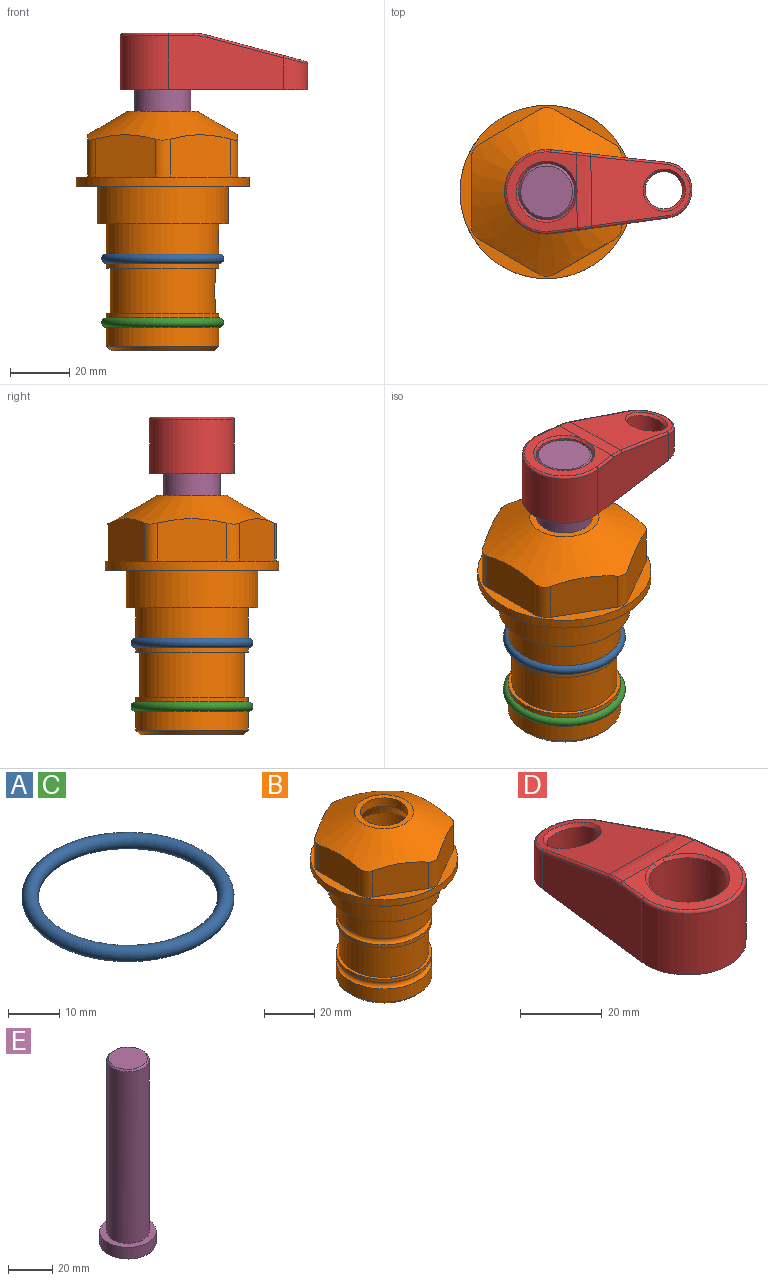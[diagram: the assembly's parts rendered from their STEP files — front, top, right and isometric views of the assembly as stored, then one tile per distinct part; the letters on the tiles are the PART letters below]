
ASSEMBLY  parts=5 mates=4
PART A: 1 faces, bbox 44.7x44.7x3.2 mm
  f0: torus R=19.05mm, axis (0,0,1), area 1193.9mm2
PART B: 36 faces, bbox 58.7x58.7x81 mm
  f0: cylinder r=17.78mm len=35.56mm, axis (0,0,1), area 1670.8mm2, adj f23,f24,f31
  f1: cylinder r=19.05mm len=38.1mm, axis (0,0,1), area 1191.9mm2, adj f26,f27,f30
  f2: plane 58.66x58.66mm, normal (0,0,-1), area 1150.6mm2, adj f3,f28
  f3: cylinder r=29.33mm len=58.66mm, axis (0,0,-1), area 585.1mm2, adj f2,f4
  f4: plane 58.66x58.66mm, normal (0,0,1), area 475.9mm2, adj f3,f5,f6,f7,f8,f9,f10,f11
  f5: plane 20.32x14.34mm, normal (-0.5,0.87,0), area 324.4mm2, adj f4,f15,f16,f17
  f6: plane 20.32x14.34mm, normal (0.5,0.87,0), area 324.4mm2, adj f4,f14,f15,f17
  f7: plane 23.48x14.34mm, normal (1,0,0), area 324.4mm2, adj f4,f13,f14,f17
  f8: plane 20.32x14.34mm, normal (0.5,-0.87,0), area 324.4mm2, adj f4,f12,f13,f17
  f9: plane 20.32x14.34mm, normal (-0.5,-0.87,0), area 324.4mm2, adj f4,f11,f12,f17
  f10: plane 23.48x14.34mm, normal (-1,0,0), area 324.4mm2, adj f4,f11,f16,f17
  f11: cylinder r=5.08mm len=12.85mm, axis (0,0,-1), area 67.2mm2, adj f4,f9,f10,f17
  f12: cylinder r=5.08mm len=12.85mm, axis (0,0,-1), area 67.2mm2, adj f4,f8,f9,f17
  f13: cylinder r=5.08mm len=12.85mm, axis (0,0,-1), area 67.2mm2, adj f4,f7,f8,f17
  f14: cylinder r=5.08mm len=12.85mm, axis (0,0,-1), area 67.2mm2, adj f4,f6,f7,f17
  f15: cylinder r=5.08mm len=12.85mm, axis (0,0,-1), area 67.2mm2, adj f4,f5,f6,f17
  f16: cylinder r=5.08mm len=12.85mm, axis (0,0,-1), area 67.2mm2, adj f4,f5,f10,f17
  f17: cone r=11.73mm half-angle=60deg, axis (0,0,-1), area 2071.8mm2, adj f5,f6,f7,f8,f9,f10,f11,f12
  f18: plane 23.46x23.46mm, normal (0,0,1), area 147.4mm2, adj f17,f35
  f19: plane 34.93x34.93mm, normal (0,0,-1), area 958mm2, adj f29
  f20: cylinder r=19.05mm len=38.1mm, axis (0,0,1), area 760.1mm2, adj f21,f29
  f21: torus R=19.05mm, axis (0,0,1), area 565.3mm2, adj f20,f22
  f22: cylinder r=19.05mm len=38.1mm, axis (0,0,1), area 190mm2, adj f21,f23
  f23: plane 38.1x38.1mm, normal (0,0,1), area 146.9mm2, adj f0,f22
  f24: plane 38.1x38.1mm, normal (0,0,-1), area 146.9mm2, adj f0,f25
  f25: cylinder r=19.05mm len=38.1mm, axis (0,0,1), area 190mm2, adj f24,f26
  f26: torus R=19.05mm, axis (0,0,1), area 565.3mm2, adj f1,f25
  f27: plane 44.45x44.45mm, normal (0,0,-1), area 411.7mm2, adj f1,f28
  f28: cylinder r=22.23mm len=44.45mm, axis (0,0,1), area 1773.5mm2, adj f2,f27
  f29: cone r=19.05mm half-angle=45deg, axis (0,0,1), area 257.5mm2, adj f19,f20
  f30: cylinder r=3.17mm len=6.75mm, axis (-1,0,0), area 128mm2, adj f1,f33
  f31: cylinder r=3.17mm len=6.35mm, axis (-1,0,0), area 102.5mm2, adj f0,f33
  f32: plane 25.4x25.4mm, normal (0,0,1), area 506.7mm2, adj f33
  f33: cylinder r=12.7mm len=66.42mm, axis (0,0,-1), area 5236.2mm2, adj f30,f31,f32,f34
  f34: cone r=9.53mm half-angle=30deg, axis (0,0,-1), area 443.4mm2, adj f33,f35
  f35: cylinder r=9.53mm len=19.05mm, axis (0,0,-1), area 240.9mm2, adj f18,f34
PART C: same geometry as A
PART D: 31 faces, bbox 31.7x65.5x19.8 mm
  f0: plane 39.12x18.26mm, normal (0.99,0.12,0), area 612.2mm2, adj f1,f4,f7,f11,f13,f15
  f1: cylinder r=9.53mm len=18.91mm, axis (0,0,-1), area 296.1mm2, adj f0,f2,f7,f17
  f2: plane 39.12x18.26mm, normal (-0.99,0.12,0), area 612.2mm2, adj f1,f4,f7,f12,f14,f16
  f3: cylinder r=6.35mm len=12.7mm, axis (0,0,-1), area 362.4mm2, adj f7,f18
  f4: cylinder r=14.29mm len=28.58mm, axis (0,0,-1), area 882.2mm2, adj f0,f2,f7,f10
  f5: cylinder r=9.53mm len=19.05mm, axis (0,0,-1), area 1092.6mm2, adj f7,f19,f20
  f6: plane 26.99x23.69mm, normal (0,0,1), area 216.2mm2, adj f9,f10,f11,f12,f19
  f7: plane 63.5x28.58mm, normal (0,0,-1), area 661.8mm2, adj f0,f1,f2,f3,f4,f5,f22,f23
  f8: plane 33.52x23.6mm, normal (0,0.26,0.97), area 486mm2, adj f9,f15,f16,f17,f18
  f9: cylinder r=19.05mm len=24.72mm, axis (1,0,0), area 120.4mm2, adj f6,f8,f13,f14,f20
  f10: torus R=13.49mm, axis (0,0,1), area 59mm2, adj f4,f6,f11,f12
  f11: cylinder r=0.79mm len=8.67mm, axis (0.12,-0.99,0), area 10.8mm2, adj f0,f6,f10,f13
  f12: cylinder r=0.79mm len=8.67mm, axis (0.12,0.99,0), area 10.8mm2, adj f2,f6,f10,f14
  f13: bspline ~4.95x1.42mm, area 6.1mm2, adj f0,f9,f11,f15
  f14: bspline ~4.95x1.42mm, area 6.1mm2, adj f2,f9,f12,f16
  f15: cylinder r=0.79mm len=25.95mm, axis (0.12,-0.96,0.26), area 32.9mm2, adj f0,f8,f13,f17
  f16: cylinder r=0.79mm len=25.95mm, axis (0.12,0.96,-0.26), area 32.9mm2, adj f2,f8,f14,f17
  f17: bspline ~18.91x8.38mm, area 30mm2, adj f1,f8,f15,f16
  f18: bspline ~14.29x14.29mm, area 48.3mm2, adj f3,f8
  f19: cone r=9.53mm half-angle=45deg, axis (0,0,1), area 66.5mm2, adj f5,f6,f20
  f20: bspline ~3.22x0.96mm, area 3.5mm2, adj f5,f9,f19
  f21: plane 2.75x2.72mm, normal (0,0,-1), area 2.9mm2, adj f23,f25,f28
  f22: plane 23.05x15.88mm, normal (-0.99,-0.12,0), area 323.6mm2, adj f7,f25,f26,f27,f28,f29
  f23: plane 23.05x15.88mm, normal (0.99,-0.12,0), area 323.6mm2, adj f7,f21,f25,f27,f28,f30
  f24: cylinder r=9.53mm len=10.69mm, axis (0,0,-1), area 114.7mm2, adj f7,f27,f29,f30
  f25: cylinder r=12.7mm len=20.59mm, axis (0,0,-1), area 381.1mm2, adj f7,f21,f22,f23,f26,f28
  f26: plane 2.75x2.72mm, normal (0,0,-1), area 2.9mm2, adj f22,f25,f28
  f27: plane 19.72x18.37mm, normal (0,-0.26,-0.97), area 291.8mm2, adj f22,f23,f24,f28,f29,f30
  f28: cylinder r=15.88mm len=19.92mm, axis (1,0,0), area 54.8mm2, adj f21,f22,f23,f25,f26,f27
  f29: cylinder r=1.59mm len=11mm, axis (0,0,-1), area 34.7mm2, adj f7,f22,f24,f27
  f30: cylinder r=1.59mm len=11mm, axis (0,0,-1), area 34.7mm2, adj f7,f23,f24,f27
PART E: 6 faces, bbox 25.4x25.4x101.6 mm
  f0: plane 17.46x17.46mm, normal (0,0,1), area 239.5mm2, adj f5
  f1: plane 25.4x25.4mm, normal (0,0,-1), area 506.7mm2, adj f2
  f2: cylinder r=12.7mm len=25.4mm, axis (0,0,1), area 506.7mm2, adj f1,f3
  f3: plane 25.4x25.4mm, normal (0,0,1), area 221.7mm2, adj f2,f4
  f4: cylinder r=9.53mm len=94.46mm, axis (0,0,1), area 5653mm2, adj f3,f5
  f5: cone r=8.73mm half-angle=45deg, axis (0,0,-1), area 64.4mm2, adj f0,f4
PLACE A at identity
PLACE B at identity fixed
PLACE C t=(0,0,-21.59)mm
PLACE D rot(axis=(0,0,-1),89.2deg) t=(0,0,-11.65)mm
PLACE E rot(axis=(0,0,-1),89.2deg) t=(0,0,-12.45)mm
MATE cylindrical E.f2 <-> B.f0  axis (0,0,-1) through (0,0,-50.55)mm
MATE fastened C.f0 <-> B.f0  axis (0,0,1) through (0,0,-46.1)mm
MATE fastened E.f2 <-> D.f4  axis (0,0,1) through (0,0,51.05)mm
MATE fastened A.f0 <-> B.f0  axis (0,0,1) through (0,0,-24.51)mm
